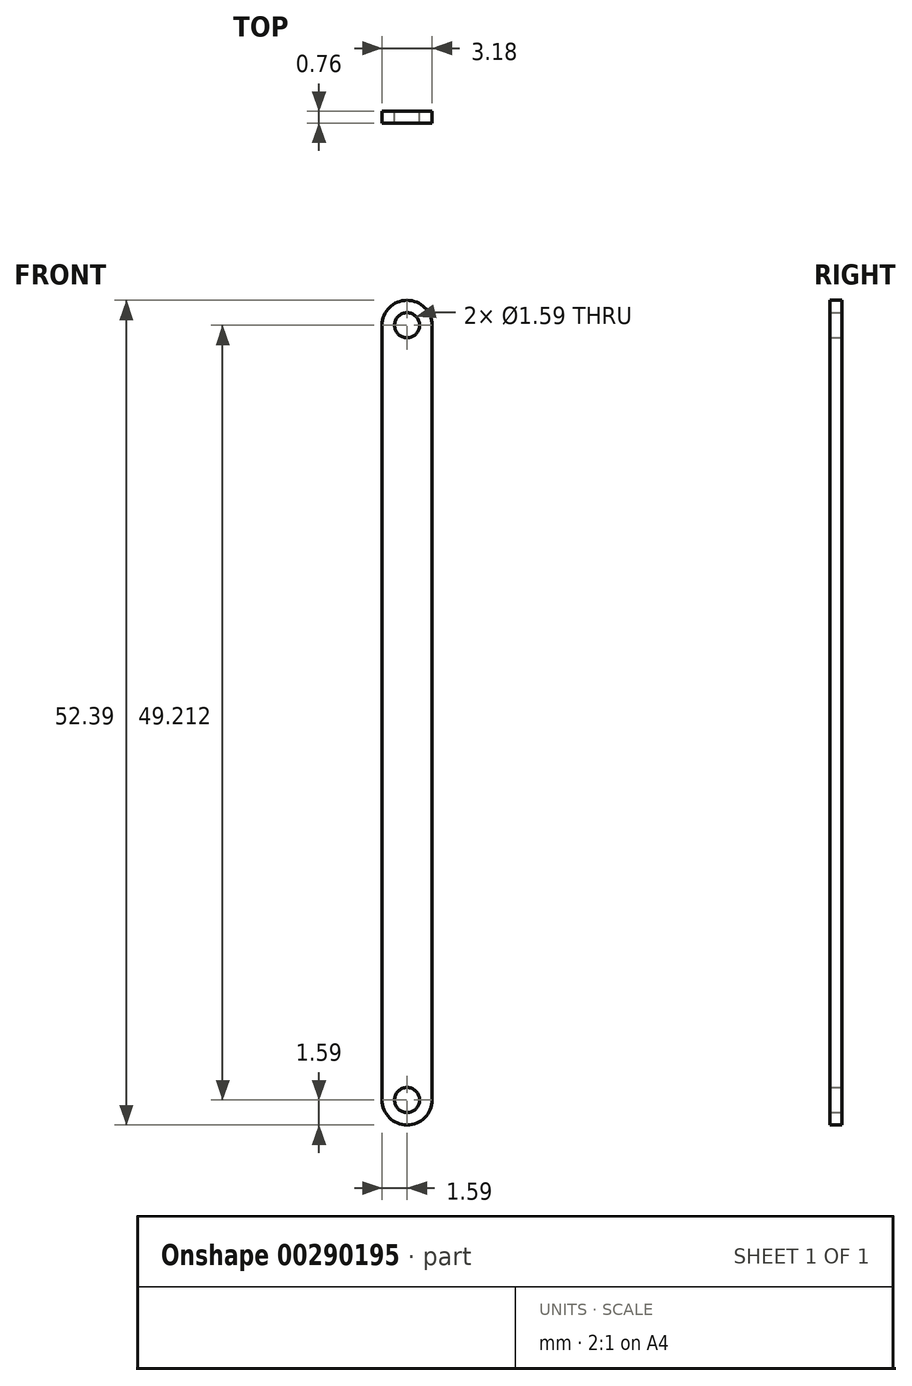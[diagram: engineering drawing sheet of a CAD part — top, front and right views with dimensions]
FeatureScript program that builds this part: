
annotation { "Feature Type Name" : "Feature", "Feature Type Description" : "" }
export const myFeature = defineFeature(function(context is Context, id is Id, definition is map)
    precondition{}
    {
        {
            var Q0;
            Q0=qCreatedBy(makeId("Front.planeOp"),FACE);
            var sketch = newSketch(context, id + "F0", { "sketchPlane" : qUnion([Q0])});
            skLineSegment(sketch, "E0", {"start": v(0, 0) * mm, "end": v(0, 49.21) * mm, "construction": true});
            skArc(sketch, "E1.0.startCap", {"start": v(1.59, 0) * mm, "mid": v(0, -1.59) * mm, "end": v(-1.59, 0) * mm});
            skArc(sketch, "E1.0.endCap", {"start": v(-1.59, 49.21) * mm, "mid": v(0, 50.8) * mm, "end": v(1.59, 49.21) * mm});
            skLineSegment(sketch, "E1.0.left", {"start": v(-1.59, 0) * mm, "end": v(-1.59, 49.21) * mm});
            skLineSegment(sketch, "E1.0.right", {"start": v(1.59, 0) * mm, "end": v(1.59, 49.21) * mm});
            skCircle(sketch, "E2", {"center": v(0, 0) * mm, "radius": 0.8 * mm});
            skCircle(sketch, "E3", {"center": v(0, 49.21) * mm, "radius": 0.8 * mm});
            skSolve(sketch);
        }
        {
            var Q0;
            Q0 = qSketchRegion(id + "F0", true);
            extrude(context, id + "F1", {"entities" : qUnion([Q0]), "endBound" : BoundingType.SYMMETRIC, "depth" : 0.76 * mm});
        }
    });
